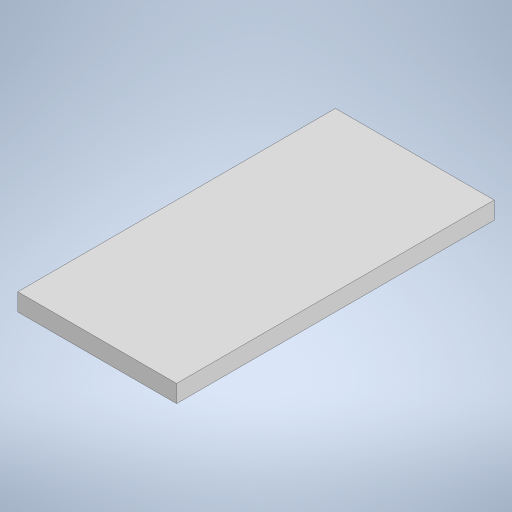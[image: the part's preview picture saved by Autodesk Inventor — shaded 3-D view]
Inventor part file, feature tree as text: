
AUTODESK INVENTOR PART (.ipt)
format: ipt  version: 2023 (Build 270158000, 158)  size: 200,192 bytes
history: native  units: mm
features: extrude x1, sketch x1
ambient origin geometry x8: Origin, YZ Plane, XZ Plane, XY Plane, X Axis, Y Axis, Z Axis, Center Point
bodies: Solid1 (feature_tree)
feature tree (2):
  extrude  "Extrusion1"  Depth=50.0mm
  sketch  "Sketch1"  dims[d0=100.0mm d1=50.0mm d2=5.5mm d3=0.0mm]
